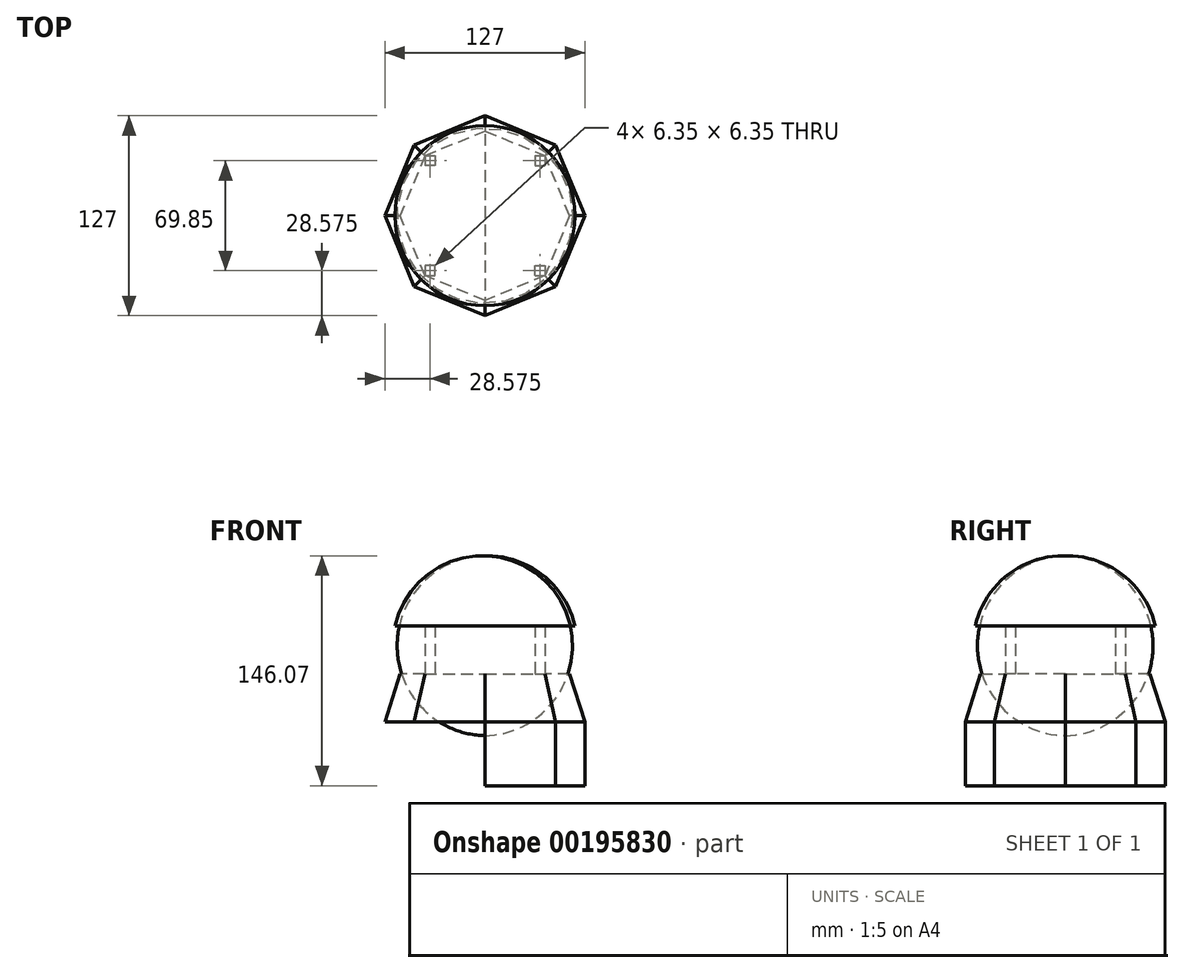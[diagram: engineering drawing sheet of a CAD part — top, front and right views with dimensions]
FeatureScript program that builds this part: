
annotation { "Feature Type Name" : "Feature", "Feature Type Description" : "" }
export const myFeature = defineFeature(function(context is Context, id is Id, definition is map)
    precondition{}
    {
        {
            var Q0;
            Q0=qCreatedBy(makeId("Top.planeOp"),FACE);
            cPlane(context, id + "F0", {"entities" : qUnion([Q0]), "cplaneType" : CPlaneType.OFFSET, "offset" : 40.64 * mm, "width" : 152.4 * mm, "height" : 152.4 * mm});
        }
        {
            var Q0;
            Q0=qCreatedBy(makeId("Top.planeOp"),FACE);
            var sketch = newSketch(context, id + "F1", { "sketchPlane" : qUnion([Q0])});
            skArc(sketch, "E0", {"start": v(0, -63.5) * mm, "mid": v(63.5, 0) * mm, "end": v(0, 63.5) * mm, "construction": true});
            skLineSegment(sketch, "E1", {"start": v(0, 63.5) * mm, "end": v(0, -63.5) * mm});
            skLineSegment(sketch, "E2", {"start": v(0, 0) * mm, "end": v(44.9, 44.9) * mm, "construction": true});
            skLineSegment(sketch, "E3", {"start": v(0, 63.5) * mm, "end": v(44.9, 44.9) * mm});
            skLineSegment(sketch, "E4", {"start": v(63.5, 0) * mm, "end": v(44.9, 44.9) * mm});
            skLineSegment(sketch, "E5", {"start": v(63.5, 0) * mm, "end": v(44.9, -44.9) * mm});
            skLineSegment(sketch, "E6", {"start": v(44.9, -44.9) * mm, "end": v(0, -63.5) * mm});
            skLineSegment(sketch, "E7", {"start": v(0, 0) * mm, "end": v(63.5, 0) * mm, "construction": true});
            skLineSegment(sketch, "E8", {"start": v(0, 0) * mm, "end": v(44.9, -44.9) * mm, "construction": true});
            skSolve(sketch);
        }
        {
            var Q0;
            Q0=makeQuery(id+"F1.imprint","IMPRINT",FACE,{"disambiguationData":[TD([[makeQuery(id+"F1.imprint","IMPRINT",EDGE,{"derivedFrom":sQuery(id+"F1.wireOp",EDGE,"E1")}),1.0]])]});
            extrude(context, id + "F2", {"entities" : qUnion([Q0]), "depth" : 40.64 * mm});
        }
        {
            var Q0;
            Q0=qCreatedBy(id+"F0.planeOp",FACE);
            var sketch = newSketch(context, id + "F3", { "sketchPlane" : qUnion([Q0])});
            skCircle(sketch, "E9", {"center": v(0, 0) * mm, "radius": 63.5 * mm, "construction": true});
            skLineSegment(sketch, "E10.0", {"start": v(44.9, -44.9) * mm, "end": v(0, -63.5) * mm});
            skLineSegment(sketch, "E11.0", {"start": v(63.5, 0) * mm, "end": v(44.9, -44.9) * mm});
            skLineSegment(sketch, "E12.0", {"start": v(63.5, 0) * mm, "end": v(44.9, 44.9) * mm});
            skLineSegment(sketch, "E13.0", {"start": v(0, 63.5) * mm, "end": v(44.9, 44.9) * mm});
            skLineSegment(sketch, "E14.0", {"start": v(0, 63.5) * mm, "end": v(0, -63.5) * mm, "construction": true});
            skLineSegment(sketch, "E15", {"start": v(0, 63.5) * mm, "end": v(-44.9, 44.9) * mm});
            skLineSegment(sketch, "E16", {"start": v(-44.9, 44.9) * mm, "end": v(-63.5, 0) * mm});
            skLineSegment(sketch, "E17", {"start": v(-63.5, 0) * mm, "end": v(-44.9, -44.9) * mm});
            skLineSegment(sketch, "E18", {"start": v(-44.9, -44.9) * mm, "end": v(0, -63.5) * mm});
            skSolve(sketch);
        }
        {
            var Q0;
            Q0=qCreatedBy(id+"F0.planeOp",FACE);
            cPlane(context, id + "F4", {"entities" : qUnion([Q0]), "cplaneType" : CPlaneType.OFFSET, "offset" : 30.48 * mm, "width" : 152.4 * mm, "height" : 152.4 * mm});
        }
        {
            var Q0;
            Q0=qCreatedBy(id+"F4.planeOp",FACE);
            var sketch = newSketch(context, id + "F5", { "sketchPlane" : qUnion([Q0])});
            skLineSegment(sketch, "E19.bottom", {"start": v(-38.1, 38.1) * mm, "end": v(38.1, 38.1) * mm, "construction": true});
            skLineSegment(sketch, "E19.top", {"start": v(-38.1, -38.1) * mm, "end": v(38.1, -38.1) * mm, "construction": true});
            skLineSegment(sketch, "E19.left", {"start": v(-38.1, 38.1) * mm, "end": v(-38.1, -38.1) * mm, "construction": true});
            skLineSegment(sketch, "E19.right", {"start": v(38.1, 38.1) * mm, "end": v(38.1, -38.1) * mm, "construction": true});
            skPoint(sketch, "E19.middle", {"position": v(0, 0) * mm});
            skCircle(sketch, "E20", {"center": v(0, 0) * mm, "radius": 53.88 * mm, "construction": true});
            skLineSegment(sketch, "E21", {"start": v(-38.1, 38.1) * mm, "end": v(0, 53.88) * mm});
            skLineSegment(sketch, "E22", {"start": v(0, 53.88) * mm, "end": v(38.1, 38.1) * mm});
            skLineSegment(sketch, "E23", {"start": v(53.88, 0) * mm, "end": v(38.1, 38.1) * mm});
            skLineSegment(sketch, "E24", {"start": v(53.88, 0) * mm, "end": v(38.1, -38.1) * mm});
            skLineSegment(sketch, "E25", {"start": v(0, -53.88) * mm, "end": v(-38.1, -38.1) * mm});
            skLineSegment(sketch, "E26", {"start": v(-38.1, -38.1) * mm, "end": v(-53.88, 0) * mm});
            skLineSegment(sketch, "E27", {"start": v(-38.1, 38.1) * mm, "end": v(-53.88, 0) * mm});
            skLineSegment(sketch, "E28", {"start": v(38.1, -38.1) * mm, "end": v(0, -53.88) * mm});
            skSolve(sketch);
        }
        {
            var Q1;
            Q1 = qSketchRegion(id + "F3", true);
            var Q2;
            Q2 = qSketchRegion(id + "F5", true);
            loft(context, id + "F6", {"operationType" : NewBodyOperationType.ADD, "sheetProfilesArray" : [{ "sheetProfileEntities" : qUnion([Q1]) }, { "sheetProfileEntities" : qUnion([Q2]) }]});
        }
        {
            var Q0;
            Q0=qCreatedBy(id+"F4.planeOp",FACE);
            var sketch = newSketch(context, id + "F7", { "sketchPlane" : qUnion([Q0])});
            skLineSegment(sketch, "E29.bottom", {"start": v(-38.1, 38.1) * mm, "end": v(38.1, 38.1) * mm});
            skLineSegment(sketch, "E29.top", {"start": v(-38.1, -38.1) * mm, "end": v(38.1, -38.1) * mm});
            skLineSegment(sketch, "E29.left", {"start": v(-38.1, 38.1) * mm, "end": v(-38.1, -38.1) * mm});
            skLineSegment(sketch, "E29.right", {"start": v(38.1, 38.1) * mm, "end": v(38.1, -38.1) * mm});
            skPoint(sketch, "E29.middle", {"position": v(0, 0) * mm});
            skLineSegment(sketch, "E30", {"start": v(0, 38.1) * mm, "end": v(0, -38.1) * mm});
            skLineSegment(sketch, "E31", {"start": v(38.1, 0) * mm, "end": v(-38.1, 0) * mm});
            skLineSegment(sketch, "E32", {"start": v(-31.75, 38.1) * mm, "end": v(-31.75, 31.75) * mm});
            skLineSegment(sketch, "E33", {"start": v(-31.75, 31.75) * mm, "end": v(-38.1, 31.75) * mm});
            skLineSegment(sketch, "E34.MirrorCS", {"start": v(31.75, 38.1) * mm, "end": v(31.75, 31.75) * mm});
            skLineSegment(sketch, "E35.MirrorCS", {"start": v(31.75, 31.75) * mm, "end": v(38.1, 31.75) * mm});
            skLineSegment(sketch, "E36.MirrorCS", {"start": v(31.75, -31.75) * mm, "end": v(38.1, -31.75) * mm});
            skLineSegment(sketch, "E37.MirrorCS", {"start": v(-31.75, -38.1) * mm, "end": v(-31.75, -31.75) * mm});
            skLineSegment(sketch, "E38.MirrorCS", {"start": v(0, -38.1) * mm, "end": v(0, 38.1) * mm});
            skLineSegment(sketch, "E39.MirrorCS", {"start": v(-31.75, -31.75) * mm, "end": v(-38.1, -31.75) * mm});
            skLineSegment(sketch, "E40.MirrorCS", {"start": v(31.75, -38.1) * mm, "end": v(31.75, -31.75) * mm});
            skSolve(sketch);
        }
        {
            var Q0;
            {var subQ3=sQuery(id+"F7.wireOp",EDGE,"E32");Q0=makeQuery(id+"F7.imprint","IMPRINT",FACE,{"disambiguationData":[TD([[makeQuery(id+"F7.imprint","IMPRINT",EDGE,{"derivedFrom":subQ3}),-1.0]])]});}
            var Q1;
            {var subQ3=sQuery(id+"F7.wireOp",EDGE,"E34.MirrorCS");Q1=makeQuery(id+"F7.imprint","IMPRINT",FACE,{"disambiguationData":[TD([[makeQuery(id+"F7.imprint","IMPRINT",EDGE,{"derivedFrom":subQ3}),1.0]])]});}
            var Q2;
            {var subQ4=sQuery(id+"F7.wireOp",EDGE,"E36.MirrorCS");Q2=makeQuery(id+"F7.imprint","IMPRINT",FACE,{"disambiguationData":[TD([[makeQuery(id+"F7.imprint","IMPRINT",EDGE,{"derivedFrom":subQ4}),-1.0]])]});}
            var Q3;
            {var subQ3=sQuery(id+"F7.wireOp",EDGE,"E37.MirrorCS");Q3=makeQuery(id+"F7.imprint","IMPRINT",FACE,{"disambiguationData":[TD([[makeQuery(id+"F7.imprint","IMPRINT",EDGE,{"derivedFrom":subQ3}),1.0]])]});}
            extrude(context, id + "F8", {"entities" : qUnion([Q0, Q1, Q2, Q3]), "operationType" : NewBodyOperationType.ADD, "depth" : 30.48 * mm});
        }
        {
            var Q0;
            Q0=qCreatedBy(id+"F4.planeOp",FACE);
            cPlane(context, id + "F9", {"entities" : qUnion([Q0]), "cplaneType" : CPlaneType.OFFSET, "offset" : 30.48 * mm, "width" : 152.4 * mm, "height" : 152.4 * mm});
        }
        {
            var Q0;
            Q0=qCreatedBy(id+"F9.planeOp",FACE);
            var sketch = newSketch(context, id + "F10", { "sketchPlane" : qUnion([Q0])});
            skCircle(sketch, "E41", {"center": v(0, 0) * mm, "radius": 57.15 * mm});
            skLineSegment(sketch, "E42.0.0", {"start": v(31.75, -31.75) * mm, "end": v(38.1, -31.75) * mm, "construction": true});
            skLineSegment(sketch, "E42.0.1", {"start": v(38.1, -31.75) * mm, "end": v(38.1, -38.1) * mm, "construction": true});
            skLineSegment(sketch, "E42.0.2", {"start": v(38.1, -38.1) * mm, "end": v(53.88, 0) * mm, "construction": true});
            skLineSegment(sketch, "E42.0.3", {"start": v(53.88, 0) * mm, "end": v(38.1, 38.1) * mm, "construction": true});
            skLineSegment(sketch, "E42.0.4", {"start": v(38.1, 38.1) * mm, "end": v(38.1, 31.75) * mm, "construction": true});
            skLineSegment(sketch, "E42.0.5", {"start": v(38.1, 31.75) * mm, "end": v(31.75, 31.75) * mm, "construction": true});
            skLineSegment(sketch, "E42.0.6", {"start": v(31.75, 31.75) * mm, "end": v(31.75, 38.1) * mm, "construction": true});
            skLineSegment(sketch, "E42.0.7", {"start": v(31.75, 38.1) * mm, "end": v(38.1, 38.1) * mm, "construction": true});
            skLineSegment(sketch, "E42.0.8", {"start": v(38.1, 38.1) * mm, "end": v(0, 53.88) * mm, "construction": true});
            skLineSegment(sketch, "E42.0.9", {"start": v(0, 53.88) * mm, "end": v(-38.1, 38.1) * mm, "construction": true});
            skLineSegment(sketch, "E42.0.10", {"start": v(-38.1, 38.1) * mm, "end": v(-31.75, 38.1) * mm, "construction": true});
            skLineSegment(sketch, "E42.0.11", {"start": v(-31.75, 38.1) * mm, "end": v(-31.75, 31.75) * mm, "construction": true});
            skLineSegment(sketch, "E42.0.12", {"start": v(-31.75, 31.75) * mm, "end": v(-38.1, 31.75) * mm, "construction": true});
            skLineSegment(sketch, "E42.0.13", {"start": v(-38.1, 31.75) * mm, "end": v(-38.1, 38.1) * mm, "construction": true});
            skLineSegment(sketch, "E42.0.14", {"start": v(-38.1, 38.1) * mm, "end": v(-53.88, 0) * mm, "construction": true});
            skLineSegment(sketch, "E42.0.15", {"start": v(-53.88, 0) * mm, "end": v(-38.1, -38.1) * mm, "construction": true});
            skLineSegment(sketch, "E42.0.16", {"start": v(-38.1, -38.1) * mm, "end": v(-38.1, -31.75) * mm, "construction": true});
            skLineSegment(sketch, "E42.0.17", {"start": v(-38.1, -31.75) * mm, "end": v(-31.75, -31.75) * mm, "construction": true});
            skLineSegment(sketch, "E42.0.18", {"start": v(-31.75, -31.75) * mm, "end": v(-31.75, -38.1) * mm, "construction": true});
            skLineSegment(sketch, "E42.0.19", {"start": v(-31.75, -38.1) * mm, "end": v(-38.1, -38.1) * mm, "construction": true});
            skLineSegment(sketch, "E42.0.20", {"start": v(-38.1, -38.1) * mm, "end": v(0, -53.88) * mm, "construction": true});
            skLineSegment(sketch, "E42.0.21", {"start": v(0, -53.88) * mm, "end": v(38.1, -38.1) * mm, "construction": true});
            skLineSegment(sketch, "E42.0.22", {"start": v(38.1, -38.1) * mm, "end": v(31.75, -38.1) * mm, "construction": true});
            skLineSegment(sketch, "E42.0.23", {"start": v(31.75, -38.1) * mm, "end": v(31.75, -31.75) * mm, "construction": true});
            skLineSegment(sketch, "E43", {"start": v(0, -57.15) * mm, "end": v(-40.41, -40.41) * mm, "construction": true});
            skLineSegment(sketch, "E44", {"start": v(-40.41, -40.41) * mm, "end": v(-57.15, 0) * mm, "construction": true});
            skLineSegment(sketch, "E45", {"start": v(-57.15, 0) * mm, "end": v(-40.41, 40.41) * mm, "construction": true});
            skLineSegment(sketch, "E46", {"start": v(-40.41, 40.41) * mm, "end": v(0, 57.15) * mm, "construction": true});
            skLineSegment(sketch, "E47", {"start": v(0, 57.15) * mm, "end": v(0, 57.15) * mm});
            skLineSegment(sketch, "E48", {"start": v(0, 57.15) * mm, "end": v(40.41, 40.41) * mm, "construction": true});
            skLineSegment(sketch, "E49", {"start": v(40.41, 40.41) * mm, "end": v(57.15, 0) * mm, "construction": true});
            skLineSegment(sketch, "E50", {"start": v(57.15, 0) * mm, "end": v(40.41, -40.41) * mm, "construction": true});
            skLineSegment(sketch, "E51", {"start": v(40.41, -40.41) * mm, "end": v(0, -57.15) * mm, "construction": true});
            skLineSegment(sketch, "E52", {"start": v(0, -57.15) * mm, "end": v(0, 0) * mm, "construction": true});
            skLineSegment(sketch, "E53", {"start": v(0, 0) * mm, "end": v(57.15, 0) * mm, "construction": true});
            skSolve(sketch);
        }
        {
            var Q0;
            Q0=qCreatedBy(id+"F9.planeOp",FACE);
            cPlane(context, id + "F11", {"entities" : qUnion([Q0]), "cplaneType" : CPlaneType.OFFSET, "offset" : 15.24 * mm, "width" : 152.4 * mm, "height" : 152.4 * mm});
        }
        {
            var Q0;
            Q0=qCreatedBy(makeId("Front.planeOp"),FACE);
            var sketch = newSketch(context, id + "F12", { "sketchPlane" : qUnion([Q0])});
            skLineSegment(sketch, "E54.0", {"start": v(-57.15, 101.6) * mm, "end": v(57.15, 101.6) * mm});
            skPoint(sketch, "E55", {"position": v(0, 101.6) * mm});
            skLineSegment(sketch, "E56", {"start": v(0, 101.6) * mm, "end": v(0, 146.05) * mm});
            skArc(sketch, "E57", {"start": v(0, 146.05) * mm, "mid": v(-36.51, 134.03) * mm, "end": v(-57.15, 101.6) * mm});
            skSolve(sketch);
        }
        {
            var Q0;
            {var subQ2=sQuery(id+"F12.wireOp",EDGE,"E56");Q0=makeQuery(id+"F12.imprint","IMPRINT",FACE,{"disambiguationData":[TD([[makeQuery(id+"F12.imprint","IMPRINT",EDGE,{"derivedFrom":subQ2}),1.0]])]});}
            var Q1;
            Q1=sQuery(id+"F12.wireOp",EDGE,"E56");
            revolve(context, id + "F13", {"operationType" : NewBodyOperationType.ADD, "entities" : qUnion([Q0]), "axis" : qUnion([Q1]), "revolveType" : RevolveType.FULL});
        }
    });
